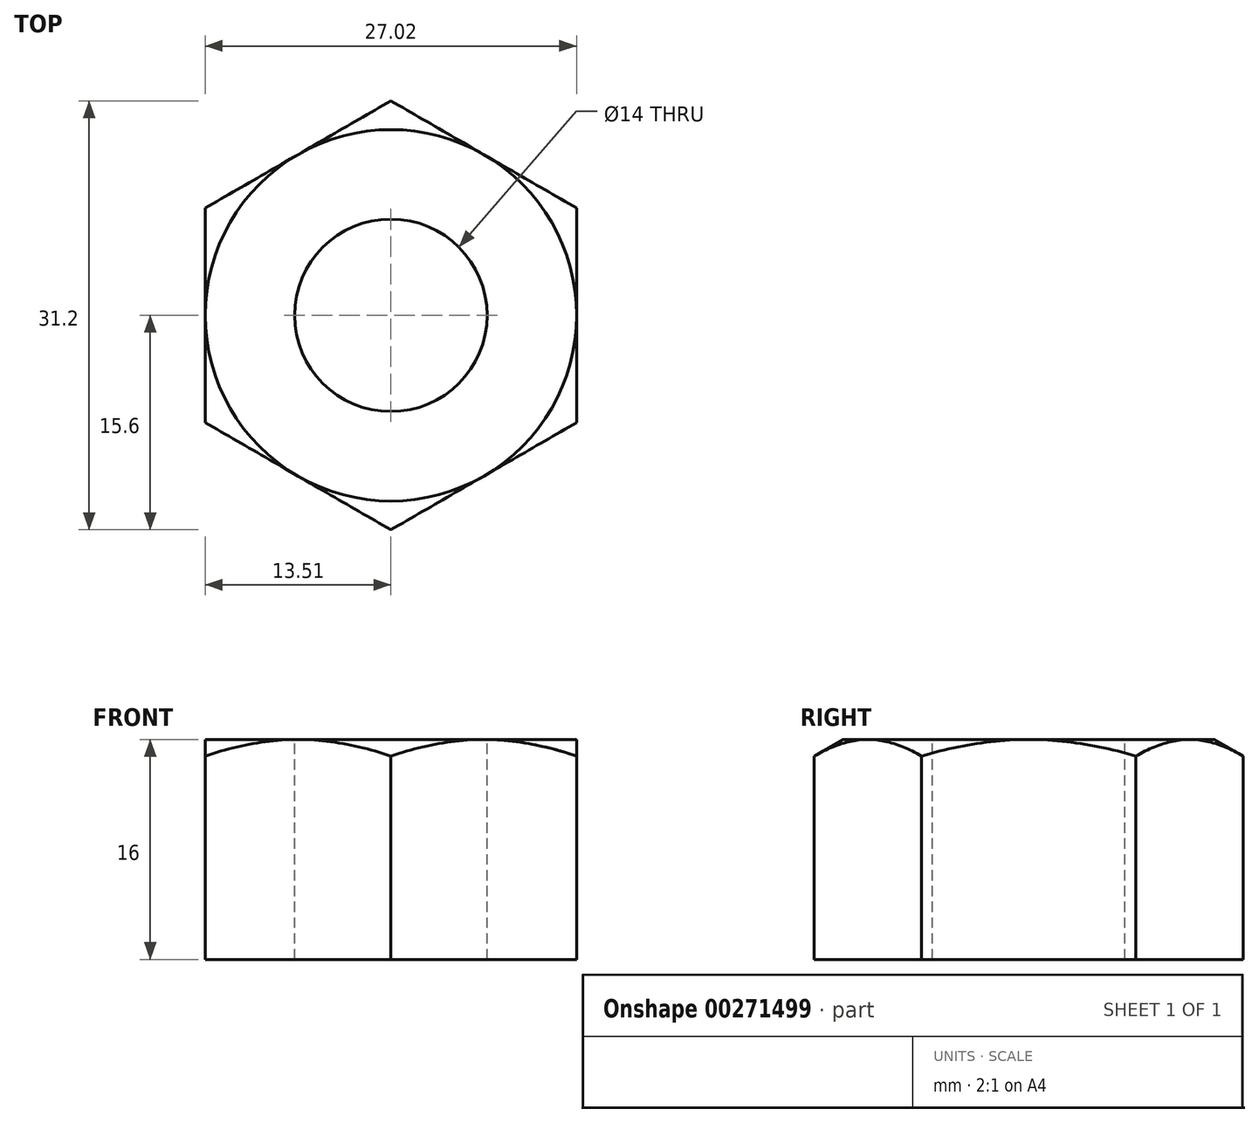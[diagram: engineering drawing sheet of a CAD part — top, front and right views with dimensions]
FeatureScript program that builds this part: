
annotation { "Feature Type Name" : "Feature", "Feature Type Description" : "" }
export const myFeature = defineFeature(function(context is Context, id is Id, definition is map)
    precondition{}
    {
        {
            var Q0;
            Q0=qCreatedBy(makeId("Top.planeOp"),FACE);
            var sketch = newSketch(context, id + "F0", { "sketchPlane" : qUnion([Q0])});
            skCircle(sketch, "E0.cCircle", {"center": v(0, 0) * mm, "radius": 15.6 * mm, "construction": true});
            skLineSegment(sketch, "E0.0", {"start": v(13.5, 7.8) * mm, "end": v(13.5, -7.8) * mm});
            skLineSegment(sketch, "E0.1", {"start": v(13.5, -7.8) * mm, "end": v(0, -15.6) * mm});
            skLineSegment(sketch, "E0.2", {"start": v(0, -15.6) * mm, "end": v(-13.5, -7.8) * mm});
            skLineSegment(sketch, "E0.3", {"start": v(-13.5, -7.8) * mm, "end": v(-13.5, 7.8) * mm});
            skLineSegment(sketch, "E0.4", {"start": v(-13.5, 7.8) * mm, "end": v(0, 15.6) * mm});
            skLineSegment(sketch, "E0.5", {"start": v(0, 15.6) * mm, "end": v(13.5, 7.8) * mm});
            skCircle(sketch, "E1", {"center": v(0, 0) * mm, "radius": 13.5 * mm, "construction": true});
            skSolve(sketch);
        }
        {
            var Q0;
            Q0 = qSketchRegion(id + "F0", true);
            extrude(context, id + "F1", {"entities" : qUnion([Q0]), "oppositeDirection" : true, "depth" : 16 * mm});
        }
        {
            var Q0;
            Q0=qCreatedBy(makeId("Front.planeOp"),FACE);
            var sketch = newSketch(context, id + "F2", { "sketchPlane" : qUnion([Q0])});
            skLineSegment(sketch, "E2", {"start": v(16, 0) * mm, "end": v(16, -1.44) * mm});
            skLineSegment(sketch, "E3", {"start": v(16, -1.44) * mm, "end": v(13.5, 0) * mm});
            skLineSegment(sketch, "E4", {"start": v(13.5, 0) * mm, "end": v(16, 0) * mm});
            skLineSegment(sketch, "E5", {"start": v(0, 0) * mm, "end": v(0, -16) * mm, "construction": true});
            skSolve(sketch);
        }
        {
            var Q0;
            Q0 = qSketchRegion(id + "F2", true);
            var Q1;
            Q1=sQuery(id+"F2.wireOp",EDGE,"E5");
            revolve(context, id + "F3", {"operationType" : NewBodyOperationType.REMOVE, "entities" : qUnion([Q0]), "axis" : qUnion([Q1]), "revolveType" : RevolveType.FULL, "oppositeDirection" : true});
        }
        {
            var Q0;
            Q0=sQuery(id+"F0.wireOp",VERTEX,"E0.cCircle.center");
            var Q1;
            Q1=makeQuery(id+"F1.opExtrude","SWEPT_BODY",BODY,{"disambiguationData":[OSD([sQuery(id+"F0.wireOp",EDGE,"E0.0"),sQuery(id+"F0.wireOp",EDGE,"E0.1"),sQuery(id+"F0.wireOp",EDGE,"E0.2"),sQuery(id+"F0.wireOp",EDGE,"E0.3"),sQuery(id+"F0.wireOp",EDGE,"E0.4"),sQuery(id+"F0.wireOp",EDGE,"E0.5")])]});
            hole(context, id + "F4", {"style" : HoleStyle.SIMPLE, "endStyle" : HoleEndStyle.THROUGH, "standardTappedOrClearance" : lookupTablePath({ "standard" : "ISO", "engagement" : "75%", "pitch" : "2 mm", "size" : "M16", "type" : "Tapped" }), "standardBlindInLast" : lookupTablePath({ "standard" : "ISO", "engagement" : "75%", "pitch" : "2 mm", "size" : "M16", "type" : "Tapped" }), "holeDiameter" : 14 * mm, "showTappedDepth" : true, "tappedDepth" : 16 * mm, "tapClearance" : 3, "locations" : qUnion([Q0]), "scope" : qUnion([Q1]), "majorDiameter" : 16 * mm});
        }
    });
